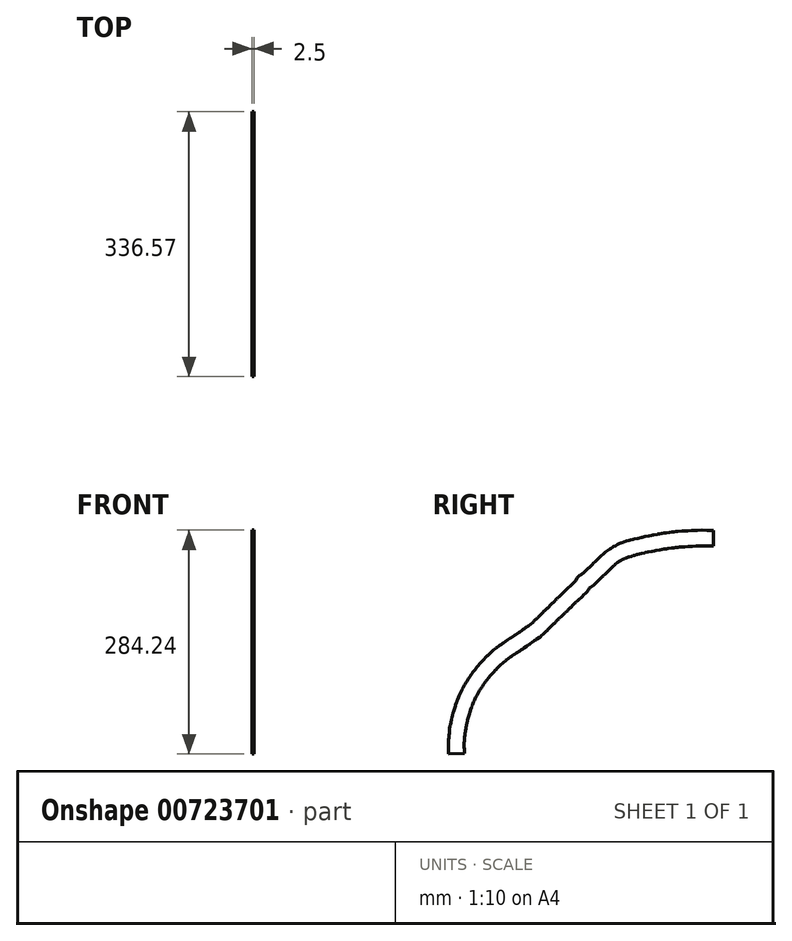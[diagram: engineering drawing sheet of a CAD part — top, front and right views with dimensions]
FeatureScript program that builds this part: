
annotation { "Feature Type Name" : "Feature", "Feature Type Description" : "" }
export const myFeature = defineFeature(function(context is Context, id is Id, definition is map)
    precondition{}
    {
        {
            var Q0;
            Q0=qCreatedBy(makeId("Right.planeOp"),FACE);
            var sketch = newSketch(context, id + "F0", { "sketchPlane" : qUnion([Q0])});
            skLineSegment(sketch, "E0", {"start": v(33.53, 90.46) * mm, "end": v(30.93, 90.49) * mm});
            skLineSegment(sketch, "E1", {"start": v(30.93, 90.49) * mm, "end": v(30.24, 90.51) * mm});
            skLineSegment(sketch, "E2", {"start": v(30.24, 90.51) * mm, "end": v(28.8, 90.52) * mm});
            skLineSegment(sketch, "E3", {"start": v(28.8, 90.52) * mm, "end": v(26.32, 90.53) * mm});
            skLineSegment(sketch, "E4", {"start": v(26.32, 90.53) * mm, "end": v(25.6, 90.55) * mm});
            skLineSegment(sketch, "E5", {"start": v(25.6, 90.55) * mm, "end": v(19.08, 90.68) * mm});
            skLineSegment(sketch, "E6", {"start": v(19.08, 90.68) * mm, "end": v(19.02, 90.69) * mm});
            skLineSegment(sketch, "E7", {"start": v(19.02, 90.69) * mm, "end": v(13.42, 90.59) * mm});
            skLineSegment(sketch, "E8", {"start": v(13.42, 90.59) * mm, "end": v(11.9, 90.54) * mm});
            skLineSegment(sketch, "E9", {"start": v(11.9, 90.54) * mm, "end": v(10.43, 90.46) * mm});
            skLineSegment(sketch, "E10", {"start": v(10.43, 90.46) * mm, "end": v(5.78, 90.2) * mm});
            skLineSegment(sketch, "E11", {"start": v(5.78, 90.2) * mm, "end": v(1.21, 89.96) * mm});
            skLineSegment(sketch, "E12", {"start": v(1.21, 89.96) * mm, "end": v(-0.32, 89.86) * mm});
            skLineSegment(sketch, "E13", {"start": v(-0.32, 89.86) * mm, "end": v(-4.18, 89.56) * mm});
            skLineSegment(sketch, "E14", {"start": v(-4.18, 89.56) * mm, "end": v(-5.7, 89.45) * mm});
            skLineSegment(sketch, "E15", {"start": v(-5.7, 89.45) * mm, "end": v(-6.3, 89.4) * mm});
            skLineSegment(sketch, "E16", {"start": v(-6.3, 89.4) * mm, "end": v(-11.27, 88.95) * mm});
            skLineSegment(sketch, "E17", {"start": v(-11.27, 88.95) * mm, "end": v(-13.82, 88.7) * mm});
            skLineSegment(sketch, "E18", {"start": v(-13.82, 88.7) * mm, "end": v(-16.76, 88.39) * mm});
            skLineSegment(sketch, "E19", {"start": v(-16.76, 88.39) * mm, "end": v(-19.11, 88.13) * mm});
            skLineSegment(sketch, "E20", {"start": v(-19.11, 88.13) * mm, "end": v(-22.27, 87.76) * mm});
            skLineSegment(sketch, "E21", {"start": v(-22.27, 87.76) * mm, "end": v(-26.3, 87.22) * mm});
            skLineSegment(sketch, "E22", {"start": v(-26.3, 87.22) * mm, "end": v(-26.85, 87.14) * mm});
            skLineSegment(sketch, "E23", {"start": v(-26.85, 87.14) * mm, "end": v(-29.15, 86.8) * mm});
            skLineSegment(sketch, "E24", {"start": v(-29.15, 86.8) * mm, "end": v(-32.05, 86.38) * mm});
            skLineSegment(sketch, "E25", {"start": v(-32.05, 86.38) * mm, "end": v(-32.6, 86.3) * mm});
            skLineSegment(sketch, "E26", {"start": v(-32.6, 86.3) * mm, "end": v(-35.02, 85.9) * mm});
            skLineSegment(sketch, "E27", {"start": v(-35.02, 85.9) * mm, "end": v(-37.36, 85.52) * mm});
            skLineSegment(sketch, "E28", {"start": v(-37.36, 85.52) * mm, "end": v(-37.8, 85.45) * mm});
            skLineSegment(sketch, "E29", {"start": v(-37.8, 85.45) * mm, "end": v(-42.07, 84.68) * mm});
            skLineSegment(sketch, "E30", {"start": v(-42.07, 84.68) * mm, "end": v(-43.27, 84.46) * mm});
            skLineSegment(sketch, "E31", {"start": v(-43.27, 84.46) * mm, "end": v(-44.9, 84.15) * mm});
            skLineSegment(sketch, "E32", {"start": v(-44.9, 84.15) * mm, "end": v(-48.4, 83.48) * mm});
            skLineSegment(sketch, "E33", {"start": v(-48.4, 83.48) * mm, "end": v(-48.64, 83.43) * mm});
            skLineSegment(sketch, "E34", {"start": v(-48.64, 83.43) * mm, "end": v(-53.46, 82.48) * mm});
            skLineSegment(sketch, "E35", {"start": v(-53.46, 82.48) * mm, "end": v(-57.1, 81.65) * mm});
            skLineSegment(sketch, "E36", {"start": v(-57.1, 81.65) * mm, "end": v(-57.32, 81.6) * mm});
            skLineSegment(sketch, "E37", {"start": v(-57.32, 81.6) * mm, "end": v(-57.86, 81.47) * mm});
            skLineSegment(sketch, "E38", {"start": v(-57.86, 81.47) * mm, "end": v(-62.43, 80.39) * mm});
            skLineSegment(sketch, "E39", {"start": v(-62.43, 80.39) * mm, "end": v(-67.54, 79.2) * mm});
            skLineSegment(sketch, "E40", {"start": v(-67.54, 79.2) * mm, "end": v(-67.94, 79.1) * mm});
            skLineSegment(sketch, "E41", {"start": v(-67.94, 79.1) * mm, "end": v(-68.38, 78.98) * mm});
            skLineSegment(sketch, "E42", {"start": v(-68.38, 78.98) * mm, "end": v(-71.8, 78.1) * mm});
            skLineSegment(sketch, "E43", {"start": v(-71.8, 78.1) * mm, "end": v(-73.85, 77.52) * mm});
            skLineSegment(sketch, "E44", {"start": v(-73.85, 77.52) * mm, "end": v(-76.71, 76.7) * mm});
            skLineSegment(sketch, "E45", {"start": v(-76.71, 76.7) * mm, "end": v(-79.95, 75.65) * mm});
            skLineSegment(sketch, "E46", {"start": v(-79.95, 75.65) * mm, "end": v(-80.9, 75.36) * mm});
            skLineSegment(sketch, "E47", {"start": v(-80.9, 75.36) * mm, "end": v(-81.62, 75.08) * mm});
            skLineSegment(sketch, "E48", {"start": v(-81.62, 75.08) * mm, "end": v(-83.96, 74.2) * mm});
            skLineSegment(sketch, "E49", {"start": v(-83.96, 74.2) * mm, "end": v(-85.7, 73.54) * mm});
            skLineSegment(sketch, "E50", {"start": v(-85.7, 73.54) * mm, "end": v(-88.1, 72.44) * mm});
            skLineSegment(sketch, "E51", {"start": v(-88.1, 72.44) * mm, "end": v(-88.82, 72.1) * mm});
            skLineSegment(sketch, "E52", {"start": v(-88.82, 72.1) * mm, "end": v(-91.06, 70.9) * mm});
            skLineSegment(sketch, "E53", {"start": v(-91.06, 70.9) * mm, "end": v(-93.3, 69.73) * mm});
            skLineSegment(sketch, "E54", {"start": v(-93.3, 69.73) * mm, "end": v(-93.94, 69.37) * mm});
            skLineSegment(sketch, "E55", {"start": v(-93.94, 69.37) * mm, "end": v(-96.91, 67.58) * mm});
            skLineSegment(sketch, "E56", {"start": v(-96.91, 67.58) * mm, "end": v(-97.91, 66.92) * mm});
            skLineSegment(sketch, "E57", {"start": v(-97.91, 66.92) * mm, "end": v(-99.73, 65.73) * mm});
            skLineSegment(sketch, "E58", {"start": v(-99.73, 65.73) * mm, "end": v(-103.65, 62.75) * mm});
            skLineSegment(sketch, "E59", {"start": v(-103.65, 62.75) * mm, "end": v(-104.37, 62.2) * mm});
            skLineSegment(sketch, "E60", {"start": v(-104.37, 62.2) * mm, "end": v(-104.76, 61.87) * mm});
            skLineSegment(sketch, "E61", {"start": v(-104.76, 61.87) * mm, "end": v(-107.03, 59.84) * mm});
            skLineSegment(sketch, "E62", {"start": v(-107.03, 59.84) * mm, "end": v(-108.82, 58.24) * mm});
            skLineSegment(sketch, "E63", {"start": v(-108.82, 58.24) * mm, "end": v(-109.39, 57.7) * mm});
            skLineSegment(sketch, "E64", {"start": v(-109.39, 57.7) * mm, "end": v(-111.88, 55.17) * mm});
            skLineSegment(sketch, "E65", {"start": v(-111.88, 55.17) * mm, "end": v(-113.83, 53.32) * mm});
            skLineSegment(sketch, "E66", {"start": v(-113.83, 53.32) * mm, "end": v(-115.13, 52.03) * mm});
            skLineSegment(sketch, "E67", {"start": v(-115.13, 52.03) * mm, "end": v(-117.1, 50.1) * mm});
            skLineSegment(sketch, "E68", {"start": v(-117.1, 50.1) * mm, "end": v(-118.53, 48.75) * mm});
            skLineSegment(sketch, "E69", {"start": v(-118.53, 48.75) * mm, "end": v(-120.34, 46.8) * mm});
            skLineSegment(sketch, "E70", {"start": v(-120.34, 46.8) * mm, "end": v(-120.6, 46.54) * mm});
            skLineSegment(sketch, "E71", {"start": v(-120.6, 46.54) * mm, "end": v(-121.09, 46.06) * mm});
            skLineSegment(sketch, "E72", {"start": v(-121.09, 46.06) * mm, "end": v(-122.3, 44.89) * mm});
            skLineSegment(sketch, "E73", {"start": v(-122.3, 44.89) * mm, "end": v(-122.64, 44.58) * mm});
            skLineSegment(sketch, "E74", {"start": v(-122.64, 44.58) * mm, "end": v(-124.64, 42.85) * mm});
            skLineSegment(sketch, "E75", {"start": v(-124.64, 42.85) * mm, "end": v(-125.11, 42.39) * mm});
            skLineSegment(sketch, "E76", {"start": v(-125.11, 42.39) * mm, "end": v(-127.7, 39.88) * mm});
            skLineSegment(sketch, "E77", {"start": v(-127.7, 39.88) * mm, "end": v(-127.7, 39.87) * mm});
            skLineSegment(sketch, "E78", {"start": v(-127.7, 39.87) * mm, "end": v(-127.73, 39.84) * mm});
            skLineSegment(sketch, "E79", {"start": v(-127.73, 39.84) * mm, "end": v(-129.62, 37.92) * mm});
            skLineSegment(sketch, "E80", {"start": v(-129.62, 37.92) * mm, "end": v(-130.9, 36.75) * mm});
            skLineSegment(sketch, "E81", {"start": v(-130.9, 36.75) * mm, "end": v(-132.11, 35.87) * mm});
            skLineSegment(sketch, "E82", {"start": v(-132.11, 35.87) * mm, "end": v(-132.87, 35.4) * mm});
            skLineSegment(sketch, "E83", {"start": v(-132.87, 35.4) * mm, "end": v(-134.36, 34.6) * mm});
            skLineSegment(sketch, "E84", {"start": v(-134.36, 34.6) * mm, "end": v(-135.44, 34.01) * mm});
            skLineSegment(sketch, "E85", {"start": v(-135.44, 34.01) * mm, "end": v(-136.06, 33.5) * mm});
            skLineSegment(sketch, "E86", {"start": v(-136.06, 33.5) * mm, "end": v(-137.54, 32.24) * mm});
            skLineSegment(sketch, "E87", {"start": v(-137.54, 32.24) * mm, "end": v(-139.2, 30.45) * mm});
            skLineSegment(sketch, "E88", {"start": v(-139.2, 30.45) * mm, "end": v(-139.5, 30.13) * mm});
            skLineSegment(sketch, "E89", {"start": v(-139.5, 30.13) * mm, "end": v(-139.63, 29.94) * mm});
            skLineSegment(sketch, "E90", {"start": v(-139.63, 29.94) * mm, "end": v(-141.33, 26.88) * mm});
            skLineSegment(sketch, "E91", {"start": v(-141.33, 26.88) * mm, "end": v(-141.68, 26.23) * mm});
            skLineSegment(sketch, "E92", {"start": v(-141.68, 26.23) * mm, "end": v(-142.57, 25.26) * mm});
            skLineSegment(sketch, "E93", {"start": v(-142.57, 25.26) * mm, "end": v(-143.43, 24.32) * mm});
            skLineSegment(sketch, "E94", {"start": v(-143.43, 24.32) * mm, "end": v(-144.29, 23.52) * mm});
            skLineSegment(sketch, "E95", {"start": v(-144.29, 23.52) * mm, "end": v(-145.5, 22.4) * mm});
            skLineSegment(sketch, "E96", {"start": v(-145.5, 22.4) * mm, "end": v(-146.23, 21.72) * mm});
            skLineSegment(sketch, "E97", {"start": v(-146.23, 21.72) * mm, "end": v(-148.74, 19.26) * mm});
            skLineSegment(sketch, "E98", {"start": v(-148.74, 19.26) * mm, "end": v(-150.31, 17.76) * mm});
            skLineSegment(sketch, "E99", {"start": v(-150.31, 17.76) * mm, "end": v(-151.57, 16.6) * mm});
            skLineSegment(sketch, "E100", {"start": v(-151.57, 16.6) * mm, "end": v(-152.44, 15.83) * mm});
            skLineSegment(sketch, "E101", {"start": v(-152.44, 15.83) * mm, "end": v(-154.53, 13.91) * mm});
            skLineSegment(sketch, "E102", {"start": v(-154.53, 13.91) * mm, "end": v(-155.2, 13.3) * mm});
            skLineSegment(sketch, "E103", {"start": v(-155.2, 13.3) * mm, "end": v(-156.46, 12.02) * mm});
            skLineSegment(sketch, "E104", {"start": v(-156.46, 12.02) * mm, "end": v(-157.73, 10.68) * mm});
            skLineSegment(sketch, "E105", {"start": v(-157.73, 10.68) * mm, "end": v(-158.57, 9.82) * mm});
            skLineSegment(sketch, "E106", {"start": v(-158.57, 9.82) * mm, "end": v(-161.2, 7.33) * mm});
            skLineSegment(sketch, "E107", {"start": v(-161.2, 7.33) * mm, "end": v(-162.07, 6.53) * mm});
            skLineSegment(sketch, "E108", {"start": v(-162.07, 6.53) * mm, "end": v(-162.54, 6.08) * mm});
            skLineSegment(sketch, "E109", {"start": v(-162.54, 6.08) * mm, "end": v(-164.37, 4.31) * mm});
            skLineSegment(sketch, "E110", {"start": v(-164.37, 4.31) * mm, "end": v(-165.1, 3.59) * mm});
            skLineSegment(sketch, "E111", {"start": v(-165.1, 3.59) * mm, "end": v(-166.2, 2.53) * mm});
            skLineSegment(sketch, "E112", {"start": v(-166.2, 2.53) * mm, "end": v(-168.59, 0.13) * mm});
            skLineSegment(sketch, "E113", {"start": v(-168.59, 0.13) * mm, "end": v(-168.6, 0.11) * mm});
            skLineSegment(sketch, "E114", {"start": v(-168.6, 0.11) * mm, "end": v(-168.62, 0.1) * mm});
            skLineSegment(sketch, "E115", {"start": v(-168.62, 0.1) * mm, "end": v(-168.64, 0.08) * mm});
            skLineSegment(sketch, "E116", {"start": v(-168.64, 0.08) * mm, "end": v(-170.38, -1.55) * mm});
            skLineSegment(sketch, "E117", {"start": v(-170.38, -1.55) * mm, "end": v(-170.89, -2.05) * mm});
            skLineSegment(sketch, "E118", {"start": v(-170.89, -2.05) * mm, "end": v(-172.54, -3.67) * mm});
            skLineSegment(sketch, "E119", {"start": v(-172.54, -3.67) * mm, "end": v(-173.2, -4.33) * mm});
            skLineSegment(sketch, "E120", {"start": v(-173.2, -4.33) * mm, "end": v(-176.22, -7.2) * mm});
            skLineSegment(sketch, "E121", {"start": v(-176.22, -7.2) * mm, "end": v(-176.93, -7.86) * mm});
            skLineSegment(sketch, "E122", {"start": v(-176.93, -7.86) * mm, "end": v(-177.87, -8.85) * mm});
            skLineSegment(sketch, "E123", {"start": v(-177.87, -8.85) * mm, "end": v(-179.99, -10.92) * mm});
            skLineSegment(sketch, "E124", {"start": v(-179.99, -10.92) * mm, "end": v(-180.97, -11.8) * mm});
            skLineSegment(sketch, "E125", {"start": v(-180.97, -11.8) * mm, "end": v(-181.36, -12.17) * mm});
            skLineSegment(sketch, "E126", {"start": v(-181.36, -12.17) * mm, "end": v(-182.74, -13.55) * mm});
            skLineSegment(sketch, "E127", {"start": v(-182.74, -13.55) * mm, "end": v(-183.7, -14.51) * mm});
            skLineSegment(sketch, "E128", {"start": v(-183.7, -14.51) * mm, "end": v(-184.45, -15.27) * mm});
            skLineSegment(sketch, "E129", {"start": v(-184.45, -15.27) * mm, "end": v(-186.33, -16.97) * mm});
            skLineSegment(sketch, "E130", {"start": v(-186.33, -16.97) * mm, "end": v(-186.8, -17.38) * mm});
            skLineSegment(sketch, "E131", {"start": v(-186.8, -17.38) * mm, "end": v(-187.05, -17.67) * mm});
            skLineSegment(sketch, "E132", {"start": v(-187.05, -17.67) * mm, "end": v(-189.35, -20.03) * mm});
            skLineSegment(sketch, "E133", {"start": v(-189.35, -20.03) * mm, "end": v(-189.72, -20.39) * mm});
            skLineSegment(sketch, "E134", {"start": v(-189.72, -20.39) * mm, "end": v(-190.87, -21.52) * mm});
            skLineSegment(sketch, "E135", {"start": v(-190.87, -21.52) * mm, "end": v(-192.03, -22.69) * mm});
            skLineSegment(sketch, "E136", {"start": v(-192.03, -22.69) * mm, "end": v(-192.31, -22.94) * mm});
            skLineSegment(sketch, "E137", {"start": v(-192.31, -22.94) * mm, "end": v(-194.12, -24.7) * mm});
            skLineSegment(sketch, "E138", {"start": v(-194.12, -24.7) * mm, "end": v(-195.25, -25.84) * mm});
            skLineSegment(sketch, "E139", {"start": v(-195.25, -25.84) * mm, "end": v(-196.46, -27.02) * mm});
            skLineSegment(sketch, "E140", {"start": v(-196.46, -27.02) * mm, "end": v(-197.94, -28.34) * mm});
            skLineSegment(sketch, "E141", {"start": v(-197.94, -28.34) * mm, "end": v(-198.59, -28.91) * mm});
            skLineSegment(sketch, "E142", {"start": v(-198.59, -28.91) * mm, "end": v(-198.92, -29.14) * mm});
            skLineSegment(sketch, "E143", {"start": v(-198.92, -29.14) * mm, "end": v(-200.73, -30.39) * mm});
            skLineSegment(sketch, "E144", {"start": v(-200.73, -30.39) * mm, "end": v(-201.46, -30.78) * mm});
            skLineSegment(sketch, "E145", {"start": v(-201.46, -30.78) * mm, "end": v(-202.51, -31.4) * mm});
            skLineSegment(sketch, "E146", {"start": v(-202.51, -31.4) * mm, "end": v(-203.09, -31.75) * mm});
            skLineSegment(sketch, "E147", {"start": v(-203.09, -31.75) * mm, "end": v(-203.61, -32.1) * mm});
            skLineSegment(sketch, "E148", {"start": v(-203.61, -32.1) * mm, "end": v(-204.84, -33.11) * mm});
            skLineSegment(sketch, "E149", {"start": v(-204.84, -33.11) * mm, "end": v(-205.6, -33.74) * mm});
            skLineSegment(sketch, "E150", {"start": v(-205.6, -33.74) * mm, "end": v(-206.12, -34.1) * mm});
            skLineSegment(sketch, "E151", {"start": v(-206.12, -34.1) * mm, "end": v(-208.37, -35.7) * mm});
            skLineSegment(sketch, "E152", {"start": v(-208.37, -35.7) * mm, "end": v(-209.9, -36.77) * mm});
            skLineSegment(sketch, "E153", {"start": v(-209.9, -36.77) * mm, "end": v(-212.23, -38.32) * mm});
            skLineSegment(sketch, "E154", {"start": v(-212.23, -38.32) * mm, "end": v(-213.26, -39.03) * mm});
            skLineSegment(sketch, "E155", {"start": v(-213.26, -39.03) * mm, "end": v(-215.6, -40.68) * mm});
            skLineSegment(sketch, "E156", {"start": v(-215.6, -40.68) * mm, "end": v(-217.93, -42.27) * mm});
            skLineSegment(sketch, "E157", {"start": v(-217.93, -42.27) * mm, "end": v(-218.6, -42.7) * mm});
            skLineSegment(sketch, "E158", {"start": v(-218.6, -42.7) * mm, "end": v(-219.25, -43.13) * mm});
            skLineSegment(sketch, "E159", {"start": v(-219.25, -43.13) * mm, "end": v(-221.65, -44.67) * mm});
            skLineSegment(sketch, "E160", {"start": v(-221.65, -44.67) * mm, "end": v(-223.8, -46.12) * mm});
            skLineSegment(sketch, "E161", {"start": v(-223.8, -46.12) * mm, "end": v(-224.4, -46.55) * mm});
            skLineSegment(sketch, "E162", {"start": v(-224.4, -46.55) * mm, "end": v(-226.3, -47.8) * mm});
            skLineSegment(sketch, "E163", {"start": v(-226.3, -47.8) * mm, "end": v(-227.76, -48.74) * mm});
            skLineSegment(sketch, "E164", {"start": v(-227.76, -48.74) * mm, "end": v(-230.66, -50.7) * mm});
            skLineSegment(sketch, "E165", {"start": v(-230.66, -50.7) * mm, "end": v(-230.87, -50.86) * mm});
            skLineSegment(sketch, "E166", {"start": v(-230.87, -50.86) * mm, "end": v(-233.37, -52.54) * mm});
            skLineSegment(sketch, "E167", {"start": v(-233.37, -52.54) * mm, "end": v(-234.32, -53.18) * mm});
            skLineSegment(sketch, "E168", {"start": v(-234.32, -53.18) * mm, "end": v(-235.9, -54.26) * mm});
            skLineSegment(sketch, "E169", {"start": v(-235.9, -54.26) * mm, "end": v(-238.1, -55.9) * mm});
            skLineSegment(sketch, "E170", {"start": v(-238.1, -55.9) * mm, "end": v(-239.3, -56.8) * mm});
            skLineSegment(sketch, "E171", {"start": v(-239.3, -56.8) * mm, "end": v(-241.44, -58.4) * mm});
            skLineSegment(sketch, "E172", {"start": v(-241.44, -58.4) * mm, "end": v(-242.4, -59.12) * mm});
            skLineSegment(sketch, "E173", {"start": v(-242.4, -59.12) * mm, "end": v(-242.8, -59.43) * mm});
            skLineSegment(sketch, "E174", {"start": v(-242.8, -59.43) * mm, "end": v(-243.33, -59.87) * mm});
            skLineSegment(sketch, "E175", {"start": v(-243.33, -59.87) * mm, "end": v(-246.31, -62.34) * mm});
            skLineSegment(sketch, "E176", {"start": v(-246.31, -62.34) * mm, "end": v(-247.65, -63.49) * mm});
            skLineSegment(sketch, "E177", {"start": v(-247.65, -63.49) * mm, "end": v(-249.7, -65.35) * mm});
            skLineSegment(sketch, "E178", {"start": v(-249.7, -65.35) * mm, "end": v(-251.01, -66.54) * mm});
            skLineSegment(sketch, "E179", {"start": v(-251.01, -66.54) * mm, "end": v(-251.65, -67.12) * mm});
            skLineSegment(sketch, "E180", {"start": v(-251.65, -67.12) * mm, "end": v(-253.06, -68.4) * mm});
            skLineSegment(sketch, "E181", {"start": v(-253.06, -68.4) * mm, "end": v(-254.03, -69.3) * mm});
            skLineSegment(sketch, "E182", {"start": v(-254.03, -69.3) * mm, "end": v(-255.76, -70.96) * mm});
            skLineSegment(sketch, "E183", {"start": v(-255.76, -70.96) * mm, "end": v(-257.81, -73.28) * mm});
            skLineSegment(sketch, "E184", {"start": v(-257.81, -73.28) * mm, "end": v(-257.97, -73.45) * mm});
            skLineSegment(sketch, "E185", {"start": v(-257.97, -73.45) * mm, "end": v(-258.08, -73.57) * mm});
            skLineSegment(sketch, "E186", {"start": v(-258.08, -73.57) * mm, "end": v(-259.47, -74.96) * mm});
            skLineSegment(sketch, "E187", {"start": v(-259.47, -74.96) * mm, "end": v(-260.05, -75.54) * mm});
            skLineSegment(sketch, "E188", {"start": v(-260.05, -75.54) * mm, "end": v(-261.88, -77.34) * mm});
            skLineSegment(sketch, "E189", {"start": v(-261.88, -77.34) * mm, "end": v(-261.9, -77.36) * mm});
            skLineSegment(sketch, "E190", {"start": v(-261.9, -77.36) * mm, "end": v(-263.5, -79.2) * mm});
            skLineSegment(sketch, "E191", {"start": v(-263.5, -79.2) * mm, "end": v(-264.05, -79.78) * mm});
            skLineSegment(sketch, "E192", {"start": v(-264.05, -79.78) * mm, "end": v(-264.49, -80.3) * mm});
            skLineSegment(sketch, "E193", {"start": v(-264.49, -80.3) * mm, "end": v(-265.78, -81.9) * mm});
            skLineSegment(sketch, "E194", {"start": v(-265.78, -81.9) * mm, "end": v(-267.22, -83.67) * mm});
            skLineSegment(sketch, "E195", {"start": v(-267.22, -83.67) * mm, "end": v(-267.68, -84.24) * mm});
            skLineSegment(sketch, "E196", {"start": v(-267.68, -84.24) * mm, "end": v(-270.1, -87.26) * mm});
            skLineSegment(sketch, "E197", {"start": v(-270.1, -87.26) * mm, "end": v(-271.6, -89.35) * mm});
            skLineSegment(sketch, "E198", {"start": v(-271.6, -89.35) * mm, "end": v(-272.23, -90.23) * mm});
            skLineSegment(sketch, "E199", {"start": v(-272.23, -90.23) * mm, "end": v(-272.72, -90.88) * mm});
            skLineSegment(sketch, "E200", {"start": v(-272.72, -90.88) * mm, "end": v(-274.57, -93.4) * mm});
            skLineSegment(sketch, "E201", {"start": v(-274.57, -93.4) * mm, "end": v(-274.92, -93.86) * mm});
            skLineSegment(sketch, "E202", {"start": v(-274.92, -93.86) * mm, "end": v(-274.99, -93.96) * mm});
            skLineSegment(sketch, "E203", {"start": v(-274.99, -93.96) * mm, "end": v(-275.25, -94.35) * mm});
            skLineSegment(sketch, "E204", {"start": v(-275.25, -94.35) * mm, "end": v(-276.94, -96.85) * mm});
            skLineSegment(sketch, "E205", {"start": v(-276.94, -96.85) * mm, "end": v(-277.49, -97.74) * mm});
            skLineSegment(sketch, "E206", {"start": v(-277.49, -97.74) * mm, "end": v(-278.34, -99.1) * mm});
            skLineSegment(sketch, "E207", {"start": v(-278.34, -99.1) * mm, "end": v(-279.14, -100.4) * mm});
            skLineSegment(sketch, "E208", {"start": v(-279.14, -100.4) * mm, "end": v(-279.79, -101.44) * mm});
            skLineSegment(sketch, "E209", {"start": v(-279.79, -101.44) * mm, "end": v(-280.56, -102.65) * mm});
            skLineSegment(sketch, "E210", {"start": v(-280.56, -102.65) * mm, "end": v(-282.26, -105.53) * mm});
            skLineSegment(sketch, "E211", {"start": v(-282.26, -105.53) * mm, "end": v(-282.37, -105.71) * mm});
            skLineSegment(sketch, "E212", {"start": v(-282.37, -105.71) * mm, "end": v(-282.4, -105.77) * mm});
            skLineSegment(sketch, "E213", {"start": v(-282.4, -105.77) * mm, "end": v(-282.44, -105.84) * mm});
            skLineSegment(sketch, "E214", {"start": v(-282.44, -105.84) * mm, "end": v(-284.5, -109.68) * mm});
            skLineSegment(sketch, "E215", {"start": v(-284.5, -109.68) * mm, "end": v(-285.54, -111.66) * mm});
            skLineSegment(sketch, "E216", {"start": v(-285.54, -111.66) * mm, "end": v(-285.92, -112.4) * mm});
            skLineSegment(sketch, "E217", {"start": v(-285.92, -112.4) * mm, "end": v(-286.37, -113.3) * mm});
            skLineSegment(sketch, "E218", {"start": v(-286.37, -113.3) * mm, "end": v(-288.3, -117.35) * mm});
            skLineSegment(sketch, "E219", {"start": v(-288.3, -117.35) * mm, "end": v(-289.36, -119.64) * mm});
            skLineSegment(sketch, "E220", {"start": v(-289.36, -119.64) * mm, "end": v(-289.51, -120) * mm});
            skLineSegment(sketch, "E221", {"start": v(-289.51, -120) * mm, "end": v(-291.14, -123.98) * mm});
            skLineSegment(sketch, "E222", {"start": v(-291.14, -123.98) * mm, "end": v(-291.23, -124.2) * mm});
            skLineSegment(sketch, "E223", {"start": v(-291.23, -124.2) * mm, "end": v(-291.33, -124.44) * mm});
            skLineSegment(sketch, "E224", {"start": v(-291.33, -124.44) * mm, "end": v(-292.34, -127.1) * mm});
            skLineSegment(sketch, "E225", {"start": v(-292.34, -127.1) * mm, "end": v(-292.62, -127.9) * mm});
            skLineSegment(sketch, "E226", {"start": v(-292.62, -127.9) * mm, "end": v(-293.95, -131.51) * mm});
            skLineSegment(sketch, "E227", {"start": v(-293.95, -131.51) * mm, "end": v(-294.31, -132.65) * mm});
            skLineSegment(sketch, "E228", {"start": v(-294.31, -132.65) * mm, "end": v(-294.89, -134.53) * mm});
            skLineSegment(sketch, "E229", {"start": v(-294.89, -134.53) * mm, "end": v(-295.52, -136.49) * mm});
            skLineSegment(sketch, "E230", {"start": v(-295.52, -136.49) * mm, "end": v(-296.83, -140.34) * mm});
            skLineSegment(sketch, "E231", {"start": v(-296.83, -140.34) * mm, "end": v(-296.9, -140.54) * mm});
            skLineSegment(sketch, "E232", {"start": v(-296.9, -140.54) * mm, "end": v(-296.92, -140.62) * mm});
            skLineSegment(sketch, "E233", {"start": v(-296.92, -140.62) * mm, "end": v(-297.02, -140.99) * mm});
            skLineSegment(sketch, "E234", {"start": v(-297.02, -140.99) * mm, "end": v(-298.17, -145.25) * mm});
            skLineSegment(sketch, "E235", {"start": v(-298.17, -145.25) * mm, "end": v(-298.53, -146.64) * mm});
            skLineSegment(sketch, "E236", {"start": v(-298.53, -146.64) * mm, "end": v(-299.32, -150.1) * mm});
            skLineSegment(sketch, "E237", {"start": v(-299.32, -150.1) * mm, "end": v(-299.9, -152.89) * mm});
            skLineSegment(sketch, "E238", {"start": v(-299.9, -152.89) * mm, "end": v(-300.02, -153.5) * mm});
            skLineSegment(sketch, "E239", {"start": v(-300.02, -153.5) * mm, "end": v(-300.08, -153.86) * mm});
            skLineSegment(sketch, "E240", {"start": v(-300.08, -153.86) * mm, "end": v(-300.56, -156.5) * mm});
            skLineSegment(sketch, "E241", {"start": v(-300.56, -156.5) * mm, "end": v(-300.7, -157.23) * mm});
            skLineSegment(sketch, "E242", {"start": v(-300.7, -157.23) * mm, "end": v(-300.73, -157.4) * mm});
            skLineSegment(sketch, "E243", {"start": v(-300.73, -157.4) * mm, "end": v(-300.79, -157.77) * mm});
            skLineSegment(sketch, "E244", {"start": v(-300.79, -157.77) * mm, "end": v(-301.42, -161.4) * mm});
            skLineSegment(sketch, "E245", {"start": v(-301.42, -161.4) * mm, "end": v(-301.6, -162.94) * mm});
            skLineSegment(sketch, "E246", {"start": v(-301.6, -162.94) * mm, "end": v(-301.83, -165.56) * mm});
            skLineSegment(sketch, "E247", {"start": v(-301.83, -165.56) * mm, "end": v(-301.98, -167.04) * mm});
            skLineSegment(sketch, "E248", {"start": v(-301.98, -167.04) * mm, "end": v(-302.35, -170.34) * mm});
            skLineSegment(sketch, "E249", {"start": v(-302.35, -170.34) * mm, "end": v(-302.44, -171.17) * mm});
            skLineSegment(sketch, "E250", {"start": v(-302.44, -171.17) * mm, "end": v(-302.62, -173.26) * mm});
            skLineSegment(sketch, "E251", {"start": v(-302.62, -173.26) * mm, "end": v(-302.8, -175.34) * mm});
            skLineSegment(sketch, "E252", {"start": v(-302.8, -175.34) * mm, "end": v(-303, -179.07) * mm});
            skLineSegment(sketch, "E253", {"start": v(-303, -179.07) * mm, "end": v(-303.01, -179.53) * mm});
            skLineSegment(sketch, "E254", {"start": v(-303.01, -179.53) * mm, "end": v(-303.03, -180.12) * mm});
            skLineSegment(sketch, "E255", {"start": v(-303.03, -180.12) * mm, "end": v(-303.04, -183.17) * mm});
            skLineSegment(sketch, "E256", {"start": v(-303.04, -183.17) * mm, "end": v(-303.03, -184.47) * mm});
            skLineSegment(sketch, "E257", {"start": v(-303.03, -184.47) * mm, "end": v(-303.02, -185.88) * mm});
            skLineSegment(sketch, "E258", {"start": v(-303.02, -185.88) * mm, "end": v(-302.88, -188.2) * mm});
            skLineSegment(sketch, "E259", {"start": v(-302.88, -188.2) * mm, "end": v(-302.8, -189.69) * mm});
            skLineSegment(sketch, "E260", {"start": v(-302.8, -189.69) * mm, "end": v(-302.78, -191.1) * mm});
            skLineSegment(sketch, "E261", {"start": v(-302.78, -191.1) * mm, "end": v(-302.74, -193.55) * mm});
            skLineSegment(sketch, "E262.0", {"start": v(-282.79, -190.77) * mm, "end": v(-282.75, -193.23) * mm});
            skLineSegment(sketch, "E262.1", {"start": v(-282.82, -189.04) * mm, "end": v(-282.79, -190.77) * mm});
            skLineSegment(sketch, "E262.2", {"start": v(-282.9, -187.1) * mm, "end": v(-282.82, -189.04) * mm});
            skLineSegment(sketch, "E262.3", {"start": v(-283.02, -185.23) * mm, "end": v(-282.9, -187.1) * mm});
            skLineSegment(sketch, "E262.4", {"start": v(-283.03, -184.33) * mm, "end": v(-283.02, -185.23) * mm});
            skLineSegment(sketch, "E262.5", {"start": v(-283.04, -183.08) * mm, "end": v(-283.03, -184.33) * mm});
            skLineSegment(sketch, "E262.6", {"start": v(-283.04, -180.51) * mm, "end": v(-283.04, -183.08) * mm});
            skLineSegment(sketch, "E262.7", {"start": v(-283.02, -180.15) * mm, "end": v(-283.04, -180.51) * mm});
            skLineSegment(sketch, "E262.8", {"start": v(-283.01, -179.86) * mm, "end": v(-283.02, -180.15) * mm});
            skLineSegment(sketch, "E262.9", {"start": v(-282.85, -176.74) * mm, "end": v(-283.01, -179.86) * mm});
            skLineSegment(sketch, "E262.10", {"start": v(-282.7, -174.95) * mm, "end": v(-282.85, -176.74) * mm});
            skLineSegment(sketch, "E262.11", {"start": v(-282.54, -173.11) * mm, "end": v(-282.7, -174.95) * mm});
            skLineSegment(sketch, "E262.12", {"start": v(-282.48, -172.58) * mm, "end": v(-282.54, -173.11) * mm});
            skLineSegment(sketch, "E262.13", {"start": v(-282.09, -169.14) * mm, "end": v(-282.48, -172.58) * mm});
            skLineSegment(sketch, "E262.14", {"start": v(-281.92, -167.43) * mm, "end": v(-282.09, -169.14) * mm});
            skLineSegment(sketch, "E262.15", {"start": v(-281.7, -165) * mm, "end": v(-281.92, -167.43) * mm});
            skLineSegment(sketch, "E262.16", {"start": v(-281.62, -164.27) * mm, "end": v(-281.7, -165) * mm});
            skLineSegment(sketch, "E262.17", {"start": v(-281.07, -161.14) * mm, "end": v(-281.62, -164.27) * mm});
            skLineSegment(sketch, "E262.18", {"start": v(-281.01, -160.77) * mm, "end": v(-281.07, -161.14) * mm});
            skLineSegment(sketch, "E262.19", {"start": v(-281.01, -160.76) * mm, "end": v(-281.01, -160.77) * mm});
            skLineSegment(sketch, "E262.20", {"start": v(-280.89, -160.1) * mm, "end": v(-281.01, -160.76) * mm});
            skLineSegment(sketch, "E262.21", {"start": v(-280.4, -157.42) * mm, "end": v(-280.89, -160.1) * mm});
            skLineSegment(sketch, "E262.22", {"start": v(-280.37, -157.26) * mm, "end": v(-280.4, -157.42) * mm});
            skLineSegment(sketch, "E262.23", {"start": v(-280.3, -156.87) * mm, "end": v(-280.37, -157.26) * mm});
            skLineSegment(sketch, "E262.24", {"start": v(-279.77, -154.33) * mm, "end": v(-280.3, -156.87) * mm});
            skLineSegment(sketch, "E262.25", {"start": v(-279.11, -151.42) * mm, "end": v(-279.77, -154.33) * mm});
            skLineSegment(sketch, "E262.26", {"start": v(-278.84, -150.41) * mm, "end": v(-279.11, -151.42) * mm});
            skLineSegment(sketch, "E262.27", {"start": v(-277.75, -146.38) * mm, "end": v(-278.84, -150.41) * mm});
            skLineSegment(sketch, "E262.28", {"start": v(-276.53, -142.78) * mm, "end": v(-277.75, -146.38) * mm});
            skLineSegment(sketch, "E262.29", {"start": v(-275.81, -140.54) * mm, "end": v(-276.53, -142.78) * mm});
            skLineSegment(sketch, "E262.30", {"start": v(-275.2, -138.58) * mm, "end": v(-275.81, -140.54) * mm});
            skLineSegment(sketch, "E262.31", {"start": v(-275.01, -137.96) * mm, "end": v(-275.2, -138.58) * mm});
            skLineSegment(sketch, "E262.32", {"start": v(-273.8, -134.68) * mm, "end": v(-275.01, -137.96) * mm});
            skLineSegment(sketch, "E262.33", {"start": v(-273.56, -133.97) * mm, "end": v(-273.8, -134.68) * mm});
            skLineSegment(sketch, "E262.34", {"start": v(-272.8, -131.94) * mm, "end": v(-273.56, -133.97) * mm});
            skLineSegment(sketch, "E262.35", {"start": v(-272.77, -131.9) * mm, "end": v(-272.8, -131.94) * mm});
            skLineSegment(sketch, "E262.36", {"start": v(-272.62, -131.52) * mm, "end": v(-272.77, -131.9) * mm});
            skLineSegment(sketch, "E262.37", {"start": v(-271.06, -127.7) * mm, "end": v(-272.62, -131.52) * mm});
            skLineSegment(sketch, "E262.38", {"start": v(-270.2, -125.84) * mm, "end": v(-271.06, -127.7) * mm});
            skLineSegment(sketch, "E262.39", {"start": v(-268.39, -122.06) * mm, "end": v(-270.2, -125.84) * mm});
            skLineSegment(sketch, "E262.40", {"start": v(-143.31, -3.19) * mm, "end": v(-144.56, -4.46) * mm});
            skLineSegment(sketch, "E262.41", {"start": v(-142.1, -1.9) * mm, "end": v(-143.31, -3.19) * mm});
            skLineSegment(sketch, "E262.42", {"start": v(-141.32, -1.11) * mm, "end": v(-142.1, -1.9) * mm});
            skLineSegment(sketch, "E262.43", {"start": v(-140.98, -0.8) * mm, "end": v(-141.32, -1.11) * mm});
            skLineSegment(sketch, "E262.44", {"start": v(-139.06, 0.96) * mm, "end": v(-140.98, -0.8) * mm});
            skLineSegment(sketch, "E262.45", {"start": v(-138.14, 1.77) * mm, "end": v(-139.06, 0.96) * mm});
            skLineSegment(sketch, "E262.46", {"start": v(-136.61, 3.2) * mm, "end": v(-138.14, 1.77) * mm});
            skLineSegment(sketch, "E262.47", {"start": v(-134.85, 4.87) * mm, "end": v(-136.61, 3.2) * mm});
            skLineSegment(sketch, "E262.48", {"start": v(-132.38, 7.29) * mm, "end": v(-134.85, 4.87) * mm});
            skLineSegment(sketch, "E262.49", {"start": v(-131.87, 7.77) * mm, "end": v(-132.38, 7.29) * mm});
            skLineSegment(sketch, "E262.50", {"start": v(-130.7, 8.85) * mm, "end": v(-131.87, 7.77) * mm});
            skLineSegment(sketch, "E262.51", {"start": v(-129.2, 10.23) * mm, "end": v(-130.7, 8.85) * mm});
            skLineSegment(sketch, "E262.52", {"start": v(-127.81, 11.76) * mm, "end": v(-129.2, 10.23) * mm});
            skLineSegment(sketch, "E262.53", {"start": v(-125.29, 14.52) * mm, "end": v(-127.81, 11.76) * mm});
            skLineSegment(sketch, "E262.54", {"start": v(-123.8, 17.25) * mm, "end": v(-125.29, 14.52) * mm});
            skLineSegment(sketch, "E262.55", {"start": v(-123.55, 17.7) * mm, "end": v(-123.8, 17.25) * mm});
            skLineSegment(sketch, "E262.56", {"start": v(-122.79, 18.11) * mm, "end": v(-123.55, 17.7) * mm});
            skLineSegment(sketch, "E262.57", {"start": v(-120.93, 19.28) * mm, "end": v(-122.79, 18.11) * mm});
            skLineSegment(sketch, "E262.58", {"start": v(-118.24, 21.23) * mm, "end": v(-120.93, 19.28) * mm});
            skLineSegment(sketch, "E262.59", {"start": v(-115.73, 23.52) * mm, "end": v(-118.24, 21.23) * mm});
            skLineSegment(sketch, "E262.60", {"start": v(-113.58, 25.7) * mm, "end": v(-115.73, 23.52) * mm});
            skLineSegment(sketch, "E262.61", {"start": v(-111.2, 28.01) * mm, "end": v(-113.58, 25.7) * mm});
            skLineSegment(sketch, "E262.62", {"start": v(-111.13, 28.08) * mm, "end": v(-111.2, 28.01) * mm});
            skLineSegment(sketch, "E262.63", {"start": v(-109.3, 29.67) * mm, "end": v(-111.13, 28.08) * mm});
            skLineSegment(sketch, "E262.64", {"start": v(-108.6, 30.32) * mm, "end": v(-109.3, 29.67) * mm});
            skLineSegment(sketch, "E262.65", {"start": v(-107.15, 31.71) * mm, "end": v(-108.6, 30.32) * mm});
            skLineSegment(sketch, "E262.66", {"start": v(-106.4, 32.45) * mm, "end": v(-107.15, 31.71) * mm});
            skLineSegment(sketch, "E262.67", {"start": v(-105.84, 33.03) * mm, "end": v(-106.4, 32.45) * mm});
            skLineSegment(sketch, "E262.68", {"start": v(-104.34, 34.64) * mm, "end": v(-105.84, 33.03) * mm});
            skLineSegment(sketch, "E262.69", {"start": v(-103.22, 35.7) * mm, "end": v(-104.34, 34.64) * mm});
            skLineSegment(sketch, "E262.70", {"start": v(-101.07, 37.8) * mm, "end": v(-103.22, 35.7) * mm});
            skLineSegment(sketch, "E262.71", {"start": v(-99.9, 38.97) * mm, "end": v(-101.07, 37.8) * mm});
            skLineSegment(sketch, "E262.72", {"start": v(-97.86, 40.9) * mm, "end": v(-99.9, 38.97) * mm});
            skLineSegment(sketch, "E262.73", {"start": v(-95.4, 43.4) * mm, "end": v(-97.86, 40.9) * mm});
            skLineSegment(sketch, "E262.74", {"start": v(-95.28, 43.52) * mm, "end": v(-95.4, 43.4) * mm});
            skLineSegment(sketch, "E262.75", {"start": v(-93.7, 44.94) * mm, "end": v(-95.28, 43.52) * mm});
            skLineSegment(sketch, "E262.76", {"start": v(-91.84, 46.6) * mm, "end": v(-93.7, 44.94) * mm});
            skLineSegment(sketch, "E262.77", {"start": v(-91.5, 46.87) * mm, "end": v(-91.84, 46.6) * mm});
            skLineSegment(sketch, "E262.78", {"start": v(-88.2, 49.38) * mm, "end": v(-91.5, 46.87) * mm});
            skLineSegment(sketch, "E262.79", {"start": v(-86.9, 50.22) * mm, "end": v(-88.2, 49.38) * mm});
            skLineSegment(sketch, "E262.80", {"start": v(-86.22, 50.67) * mm, "end": v(-86.9, 50.22) * mm});
            skLineSegment(sketch, "E262.81", {"start": v(-83.81, 52.12) * mm, "end": v(-86.22, 50.67) * mm});
            skLineSegment(sketch, "E262.82", {"start": v(-83.66, 52.2) * mm, "end": v(-83.81, 52.12) * mm});
            skLineSegment(sketch, "E262.83", {"start": v(-81.7, 53.23) * mm, "end": v(-83.66, 52.2) * mm});
            skLineSegment(sketch, "E262.84", {"start": v(-79.85, 54.22) * mm, "end": v(-81.7, 53.23) * mm});
            skLineSegment(sketch, "E262.85", {"start": v(-79.68, 54.3) * mm, "end": v(-79.85, 54.22) * mm});
            skLineSegment(sketch, "E262.86", {"start": v(-77.95, 55.1) * mm, "end": v(-79.68, 54.3) * mm});
            skLineSegment(sketch, "E262.87", {"start": v(-76.88, 55.5) * mm, "end": v(-77.95, 55.1) * mm});
            skLineSegment(sketch, "E262.88", {"start": v(-74.59, 56.36) * mm, "end": v(-76.88, 55.5) * mm});
            skLineSegment(sketch, "E262.89", {"start": v(-74.36, 56.44) * mm, "end": v(-74.59, 56.36) * mm});
            skLineSegment(sketch, "E262.90", {"start": v(-23.58, 67.4) * mm, "end": v(-24.04, 67.34) * mm});
            skLineSegment(sketch, "E262.91", {"start": v(-19.8, 67.92) * mm, "end": v(-23.58, 67.4) * mm});
            skLineSegment(sketch, "E262.92", {"start": v(-16.86, 68.25) * mm, "end": v(-19.8, 67.92) * mm});
            skLineSegment(sketch, "E262.93", {"start": v(-14.57, 68.5) * mm, "end": v(-16.86, 68.25) * mm});
            skLineSegment(sketch, "E262.94", {"start": v(-11.78, 68.81) * mm, "end": v(-14.57, 68.5) * mm});
            skLineSegment(sketch, "E262.95", {"start": v(-9.41, 69.04) * mm, "end": v(-11.78, 68.81) * mm});
            skLineSegment(sketch, "E262.96", {"start": v(-4.58, 69.48) * mm, "end": v(-9.41, 69.04) * mm});
            skLineSegment(sketch, "E262.97", {"start": v(-4.14, 69.51) * mm, "end": v(-4.58, 69.48) * mm});
            skLineSegment(sketch, "E262.98", {"start": v(-2.67, 69.62) * mm, "end": v(-4.14, 69.51) * mm});
            skLineSegment(sketch, "E262.99", {"start": v(1.08, 69.91) * mm, "end": v(-2.67, 69.62) * mm});
            skLineSegment(sketch, "E262.100", {"start": v(2.38, 70) * mm, "end": v(1.08, 69.91) * mm});
            skLineSegment(sketch, "E262.101", {"start": v(6.87, 70.24) * mm, "end": v(2.38, 70) * mm});
            skLineSegment(sketch, "E262.102", {"start": v(28.71, 70.52) * mm, "end": v(26.02, 70.53) * mm});
            skLineSegment(sketch, "E262.103", {"start": v(29.85, 70.51) * mm, "end": v(28.71, 70.52) * mm});
            skLineSegment(sketch, "E262.104", {"start": v(30.49, 70.5) * mm, "end": v(29.85, 70.51) * mm});
            skLineSegment(sketch, "E262.105", {"start": v(33.32, 70.46) * mm, "end": v(30.49, 70.5) * mm});
            skLineSegment(sketch, "E262.106", {"start": v(26.02, 70.53) * mm, "end": v(25.13, 70.55) * mm});
            skLineSegment(sketch, "E262.107", {"start": v(25.13, 70.55) * mm, "end": v(18.99, 70.68) * mm});
            skLineSegment(sketch, "E262.108", {"start": v(18.99, 70.68) * mm, "end": v(13.94, 70.6) * mm});
            skLineSegment(sketch, "E262.109", {"start": v(13.94, 70.6) * mm, "end": v(12.76, 70.55) * mm});
            skLineSegment(sketch, "E262.110", {"start": v(12.76, 70.55) * mm, "end": v(11.5, 70.49) * mm});
            skLineSegment(sketch, "E262.111", {"start": v(11.5, 70.49) * mm, "end": v(6.87, 70.24) * mm});
            skLineSegment(sketch, "E262.112", {"start": v(-24.04, 67.34) * mm, "end": v(-26.24, 67.02) * mm});
            skLineSegment(sketch, "E262.113", {"start": v(-26.24, 67.02) * mm, "end": v(-29.18, 66.58) * mm});
            skLineSegment(sketch, "E262.114", {"start": v(-29.18, 66.58) * mm, "end": v(-29.57, 66.53) * mm});
            skLineSegment(sketch, "E262.115", {"start": v(-29.57, 66.53) * mm, "end": v(-31.8, 66.16) * mm});
            skLineSegment(sketch, "E262.116", {"start": v(-31.8, 66.16) * mm, "end": v(-34.07, 65.8) * mm});
            skLineSegment(sketch, "E262.117", {"start": v(-34.07, 65.8) * mm, "end": v(-34.35, 65.74) * mm});
            skLineSegment(sketch, "E262.118", {"start": v(-34.35, 65.74) * mm, "end": v(-38.48, 65) * mm});
            skLineSegment(sketch, "E262.119", {"start": v(-38.48, 65) * mm, "end": v(-39.64, 64.79) * mm});
            skLineSegment(sketch, "E262.120", {"start": v(-39.64, 64.79) * mm, "end": v(-41.19, 64.5) * mm});
            skLineSegment(sketch, "E262.121", {"start": v(-41.19, 64.5) * mm, "end": v(-44.48, 63.86) * mm});
            skLineSegment(sketch, "E262.122", {"start": v(-44.48, 63.86) * mm, "end": v(-44.7, 63.82) * mm});
            skLineSegment(sketch, "E262.123", {"start": v(-44.7, 63.82) * mm, "end": v(-49.31, 62.9) * mm});
            skLineSegment(sketch, "E262.124", {"start": v(-49.31, 62.9) * mm, "end": v(-52.64, 62.15) * mm});
            skLineSegment(sketch, "E262.125", {"start": v(-52.64, 62.15) * mm, "end": v(-52.74, 62.13) * mm});
            skLineSegment(sketch, "E262.126", {"start": v(-52.74, 62.13) * mm, "end": v(-53.22, 62.02) * mm});
            skLineSegment(sketch, "E262.127", {"start": v(-53.22, 62.02) * mm, "end": v(-57.84, 60.92) * mm});
            skLineSegment(sketch, "E262.128", {"start": v(-57.84, 60.92) * mm, "end": v(-62.84, 59.75) * mm});
            skLineSegment(sketch, "E262.129", {"start": v(-62.84, 59.75) * mm, "end": v(-63.02, 59.7) * mm});
            skLineSegment(sketch, "E262.130", {"start": v(-63.02, 59.7) * mm, "end": v(-63.38, 59.61) * mm});
            skLineSegment(sketch, "E262.131", {"start": v(-63.38, 59.61) * mm, "end": v(-66.6, 58.78) * mm});
            skLineSegment(sketch, "E262.132", {"start": v(-66.6, 58.78) * mm, "end": v(-68.4, 58.27) * mm});
            skLineSegment(sketch, "E262.133", {"start": v(-68.4, 58.27) * mm, "end": v(-70.88, 57.57) * mm});
            skLineSegment(sketch, "E262.134", {"start": v(-70.88, 57.57) * mm, "end": v(-73.88, 56.6) * mm});
            skLineSegment(sketch, "E262.135", {"start": v(-73.88, 56.6) * mm, "end": v(-74.36, 56.44) * mm});
            skLineSegment(sketch, "E262.136", {"start": v(-144.56, -4.46) * mm, "end": v(-147.5, -7.23) * mm});
            skLineSegment(sketch, "E262.137", {"start": v(-147.5, -7.23) * mm, "end": v(-148.43, -8.1) * mm});
            skLineSegment(sketch, "E262.138", {"start": v(-148.43, -8.1) * mm, "end": v(-148.8, -8.45) * mm});
            skLineSegment(sketch, "E262.139", {"start": v(-148.8, -8.45) * mm, "end": v(-150.37, -9.97) * mm});
            skLineSegment(sketch, "E262.140", {"start": v(-150.37, -9.97) * mm, "end": v(-151.1, -10.7) * mm});
            skLineSegment(sketch, "E262.141", {"start": v(-151.1, -10.7) * mm, "end": v(-152.17, -11.72) * mm});
            skLineSegment(sketch, "E262.142", {"start": v(-152.17, -11.72) * mm, "end": v(-154.29, -13.85) * mm});
            skLineSegment(sketch, "E262.143", {"start": v(-154.29, -13.85) * mm, "end": v(-154.62, -14.2) * mm});
            skLineSegment(sketch, "E262.144", {"start": v(-154.62, -14.2) * mm, "end": v(-155, -14.55) * mm});
            skLineSegment(sketch, "E262.145", {"start": v(-155, -14.55) * mm, "end": v(-156.53, -15.98) * mm});
            skLineSegment(sketch, "E262.146", {"start": v(-156.53, -15.98) * mm, "end": v(-156.88, -16.33) * mm});
            skLineSegment(sketch, "E262.147", {"start": v(-156.88, -16.33) * mm, "end": v(-158.47, -17.88) * mm});
            skLineSegment(sketch, "E262.148", {"start": v(-158.47, -17.88) * mm, "end": v(-159.25, -18.66) * mm});
            skLineSegment(sketch, "E262.149", {"start": v(-159.25, -18.66) * mm, "end": v(-162.5, -21.75) * mm});
            skLineSegment(sketch, "E262.150", {"start": v(-162.5, -21.75) * mm, "end": v(-162.87, -22.1) * mm});
            skLineSegment(sketch, "E262.151", {"start": v(-162.87, -22.1) * mm, "end": v(-163.66, -22.92) * mm});
            skLineSegment(sketch, "E262.152", {"start": v(-163.66, -22.92) * mm, "end": v(-166.32, -25.53) * mm});
            skLineSegment(sketch, "E262.153", {"start": v(-166.32, -25.53) * mm, "end": v(-167.37, -26.47) * mm});
            skLineSegment(sketch, "E262.154", {"start": v(-167.37, -26.47) * mm, "end": v(-167.38, -26.48) * mm});
            skLineSegment(sketch, "E262.155", {"start": v(-167.38, -26.48) * mm, "end": v(-168.6, -27.7) * mm});
            skLineSegment(sketch, "E262.156", {"start": v(-168.6, -27.7) * mm, "end": v(-169.5, -28.6) * mm});
            skLineSegment(sketch, "E262.157", {"start": v(-169.5, -28.6) * mm, "end": v(-170.6, -29.71) * mm});
            skLineSegment(sketch, "E262.158", {"start": v(-170.6, -29.71) * mm, "end": v(-172.87, -31.77) * mm});
            skLineSegment(sketch, "E262.159", {"start": v(-172.87, -31.77) * mm, "end": v(-175.23, -34.2) * mm});
            skLineSegment(sketch, "E262.160", {"start": v(-175.23, -34.2) * mm, "end": v(-175.73, -34.68) * mm});
            skLineSegment(sketch, "E262.161", {"start": v(-175.73, -34.68) * mm, "end": v(-176.77, -35.7) * mm});
            skLineSegment(sketch, "E262.162", {"start": v(-176.77, -35.7) * mm, "end": v(-178.16, -37.1) * mm});
            skLineSegment(sketch, "E262.163", {"start": v(-178.16, -37.1) * mm, "end": v(-178.53, -37.44) * mm});
            skLineSegment(sketch, "E262.164", {"start": v(-178.53, -37.44) * mm, "end": v(-180.06, -38.93) * mm});
            skLineSegment(sketch, "E262.165", {"start": v(-180.06, -38.93) * mm, "end": v(-181.18, -40.05) * mm});
            skLineSegment(sketch, "E262.166", {"start": v(-181.18, -40.05) * mm, "end": v(-182.82, -41.66) * mm});
            skLineSegment(sketch, "E262.167", {"start": v(-182.82, -41.66) * mm, "end": v(-184.64, -43.27) * mm});
            skLineSegment(sketch, "E262.168", {"start": v(-184.64, -43.27) * mm, "end": v(-186.25, -44.71) * mm});
            skLineSegment(sketch, "E262.169", {"start": v(-186.25, -44.71) * mm, "end": v(-187.61, -45.64) * mm});
            skLineSegment(sketch, "E262.170", {"start": v(-187.61, -45.64) * mm, "end": v(-190.3, -47.5) * mm});
            skLineSegment(sketch, "E262.171", {"start": v(-190.3, -47.5) * mm, "end": v(-191.67, -48.22) * mm});
            skLineSegment(sketch, "E262.172", {"start": v(-191.67, -48.22) * mm, "end": v(-191.89, -48.35) * mm});
            skLineSegment(sketch, "E262.173", {"start": v(-191.89, -48.35) * mm, "end": v(-192.16, -48.58) * mm});
            skLineSegment(sketch, "E262.174", {"start": v(-192.16, -48.58) * mm, "end": v(-193.46, -49.63) * mm});
            skLineSegment(sketch, "E262.175", {"start": v(-193.46, -49.63) * mm, "end": v(-194.48, -50.37) * mm});
            skLineSegment(sketch, "E262.176", {"start": v(-194.48, -50.37) * mm, "end": v(-196.86, -52.06) * mm});
            skLineSegment(sketch, "E262.177", {"start": v(-196.86, -52.06) * mm, "end": v(-198.65, -53.3) * mm});
            skLineSegment(sketch, "E262.178", {"start": v(-198.65, -53.3) * mm, "end": v(-201.02, -54.89) * mm});
            skLineSegment(sketch, "E262.179", {"start": v(-201.02, -54.89) * mm, "end": v(-201.84, -55.45) * mm});
            skLineSegment(sketch, "E262.180", {"start": v(-201.84, -55.45) * mm, "end": v(-204.2, -57.11) * mm});
            skLineSegment(sketch, "E262.181", {"start": v(-204.2, -57.11) * mm, "end": v(-206.81, -58.9) * mm});
            skLineSegment(sketch, "E262.182", {"start": v(-206.81, -58.9) * mm, "end": v(-207.7, -59.48) * mm});
            skLineSegment(sketch, "E262.183", {"start": v(-207.7, -59.48) * mm, "end": v(-208.42, -59.94) * mm});
            skLineSegment(sketch, "E262.184", {"start": v(-208.42, -59.94) * mm, "end": v(-210.65, -61.37) * mm});
            skLineSegment(sketch, "E262.185", {"start": v(-210.65, -61.37) * mm, "end": v(-212.46, -62.6) * mm});
            skLineSegment(sketch, "E262.186", {"start": v(-212.46, -62.6) * mm, "end": v(-213.19, -63.1) * mm});
            skLineSegment(sketch, "E262.187", {"start": v(-213.19, -63.1) * mm, "end": v(-215.35, -64.52) * mm});
            skLineSegment(sketch, "E262.188", {"start": v(-215.35, -64.52) * mm, "end": v(-216.67, -65.4) * mm});
            skLineSegment(sketch, "E262.189", {"start": v(-216.67, -65.4) * mm, "end": v(-219.4, -67.23) * mm});
            skLineSegment(sketch, "E262.190", {"start": v(-219.4, -67.23) * mm, "end": v(-219.61, -67.38) * mm});
            skLineSegment(sketch, "E262.191", {"start": v(-219.61, -67.38) * mm, "end": v(-222.21, -69.15) * mm});
            skLineSegment(sketch, "E262.192", {"start": v(-222.21, -69.15) * mm, "end": v(-223.13, -69.76) * mm});
            skLineSegment(sketch, "E262.193", {"start": v(-223.13, -69.76) * mm, "end": v(-224.25, -70.52) * mm});
            skLineSegment(sketch, "E262.194", {"start": v(-224.25, -70.52) * mm, "end": v(-226.1, -71.9) * mm});
            skLineSegment(sketch, "E262.195", {"start": v(-226.1, -71.9) * mm, "end": v(-227.33, -72.83) * mm});
            skLineSegment(sketch, "E262.196", {"start": v(-227.33, -72.83) * mm, "end": v(-229.45, -74.4) * mm});
            skLineSegment(sketch, "E262.197", {"start": v(-229.45, -74.4) * mm, "end": v(-230.3, -75.05) * mm});
            skLineSegment(sketch, "E262.198", {"start": v(-230.3, -75.05) * mm, "end": v(-230.38, -75.11) * mm});
            skLineSegment(sketch, "E262.199", {"start": v(-230.38, -75.11) * mm, "end": v(-230.63, -75.31) * mm});
            skLineSegment(sketch, "E262.200", {"start": v(-230.63, -75.31) * mm, "end": v(-233.41, -77.62) * mm});
            skLineSegment(sketch, "E262.201", {"start": v(-233.41, -77.62) * mm, "end": v(-234.41, -78.48) * mm});
            skLineSegment(sketch, "E262.202", {"start": v(-234.41, -78.48) * mm, "end": v(-236.27, -80.16) * mm});
            skLineSegment(sketch, "E262.203", {"start": v(-236.27, -80.16) * mm, "end": v(-237.56, -81.34) * mm});
            skLineSegment(sketch, "E262.204", {"start": v(-237.56, -81.34) * mm, "end": v(-238.17, -81.9) * mm});
            skLineSegment(sketch, "E262.205", {"start": v(-238.17, -81.9) * mm, "end": v(-239.5, -83.12) * mm});
            skLineSegment(sketch, "E262.206", {"start": v(-239.5, -83.12) * mm, "end": v(-240.34, -83.89) * mm});
            skLineSegment(sketch, "E262.207", {"start": v(-240.34, -83.89) * mm, "end": v(-241.34, -84.84) * mm});
            skLineSegment(sketch, "E262.208", {"start": v(-241.34, -84.84) * mm, "end": v(-242.94, -86.65) * mm});
            skLineSegment(sketch, "E262.209", {"start": v(-242.94, -86.65) * mm, "end": v(-243.36, -87.1) * mm});
            skLineSegment(sketch, "E262.210", {"start": v(-243.36, -87.1) * mm, "end": v(-243.76, -87.53) * mm});
            skLineSegment(sketch, "E262.211", {"start": v(-243.76, -87.53) * mm, "end": v(-245.34, -89.11) * mm});
            skLineSegment(sketch, "E262.212", {"start": v(-245.34, -89.11) * mm, "end": v(-245.98, -89.75) * mm});
            skLineSegment(sketch, "E262.213", {"start": v(-245.98, -89.75) * mm, "end": v(-247.34, -91.09) * mm});
            skLineSegment(sketch, "E262.214", {"start": v(-247.34, -91.09) * mm, "end": v(-248.65, -92.59) * mm});
            skLineSegment(sketch, "E262.215", {"start": v(-248.65, -92.59) * mm, "end": v(-249, -92.97) * mm});
            skLineSegment(sketch, "E262.216", {"start": v(-249, -92.97) * mm, "end": v(-249.04, -93.02) * mm});
            skLineSegment(sketch, "E262.217", {"start": v(-249.04, -93.02) * mm, "end": v(-250.27, -94.52) * mm});
            skLineSegment(sketch, "E262.218", {"start": v(-250.27, -94.52) * mm, "end": v(-251.66, -96.23) * mm});
            skLineSegment(sketch, "E262.219", {"start": v(-251.66, -96.23) * mm, "end": v(-252.08, -96.76) * mm});
            skLineSegment(sketch, "E262.220", {"start": v(-252.08, -96.76) * mm, "end": v(-254.17, -99.37) * mm});
            skLineSegment(sketch, "E262.221", {"start": v(-254.17, -99.37) * mm, "end": v(-255.36, -101.01) * mm});
            skLineSegment(sketch, "E262.222", {"start": v(-255.36, -101.01) * mm, "end": v(-256.12, -102.07) * mm});
            skLineSegment(sketch, "E262.223", {"start": v(-256.12, -102.07) * mm, "end": v(-256.68, -102.83) * mm});
            skLineSegment(sketch, "E262.224", {"start": v(-256.68, -102.83) * mm, "end": v(-258.46, -105.24) * mm});
            skLineSegment(sketch, "E262.225", {"start": v(-258.46, -105.24) * mm, "end": v(-258.66, -105.51) * mm});
            skLineSegment(sketch, "E262.226", {"start": v(-258.66, -105.51) * mm, "end": v(-258.68, -105.54) * mm});
            skLineSegment(sketch, "E262.227", {"start": v(-258.68, -105.54) * mm, "end": v(-260.12, -107.67) * mm});
            skLineSegment(sketch, "E262.228", {"start": v(-260.12, -107.67) * mm, "end": v(-260.47, -108.26) * mm});
            skLineSegment(sketch, "E262.229", {"start": v(-260.47, -108.26) * mm, "end": v(-261.34, -109.63) * mm});
            skLineSegment(sketch, "E262.230", {"start": v(-261.34, -109.63) * mm, "end": v(-262.13, -110.92) * mm});
            skLineSegment(sketch, "E262.231", {"start": v(-262.13, -110.92) * mm, "end": v(-262.88, -112.13) * mm});
            skLineSegment(sketch, "E262.232", {"start": v(-262.88, -112.13) * mm, "end": v(-263.53, -113.15) * mm});
            skLineSegment(sketch, "E262.233", {"start": v(-263.53, -113.15) * mm, "end": v(-264.96, -115.55) * mm});
            skLineSegment(sketch, "E262.234", {"start": v(-264.96, -115.55) * mm, "end": v(-266.84, -119.07) * mm});
            skLineSegment(sketch, "E262.235", {"start": v(-266.84, -119.07) * mm, "end": v(-267.8, -120.87) * mm});
            skLineSegment(sketch, "E262.236", {"start": v(-267.8, -120.87) * mm, "end": v(-268.06, -121.4) * mm});
            skLineSegment(sketch, "E262.237", {"start": v(-268.06, -121.4) * mm, "end": v(-268.39, -122.06) * mm});
            skLineSegment(sketch, "E263", {"start": v(33.53, 90.46) * mm, "end": v(33.32, 70.46) * mm});
            skLineSegment(sketch, "E264", {"start": v(-302.74, -193.55) * mm, "end": v(-282.75, -193.23) * mm});
            skLineSegment(sketch, "E265", {"start": v(-282.75, -193.23) * mm, "end": v(-82.77, -190) * mm});
            skLineSegment(sketch, "E266", {"start": v(-129.62, 37.92) * mm, "end": v(-141.68, 26.23) * mm});
            skSolve(sketch);
        }
        {
            var Q0;
            Q0 = qSketchRegion(id + "F0", true);
            extrude(context, id + "F1", {"entities" : qUnion([Q0]), "depth" : 2.5 * mm, "offsetDistance" : 25 * mm});
        }
    });
